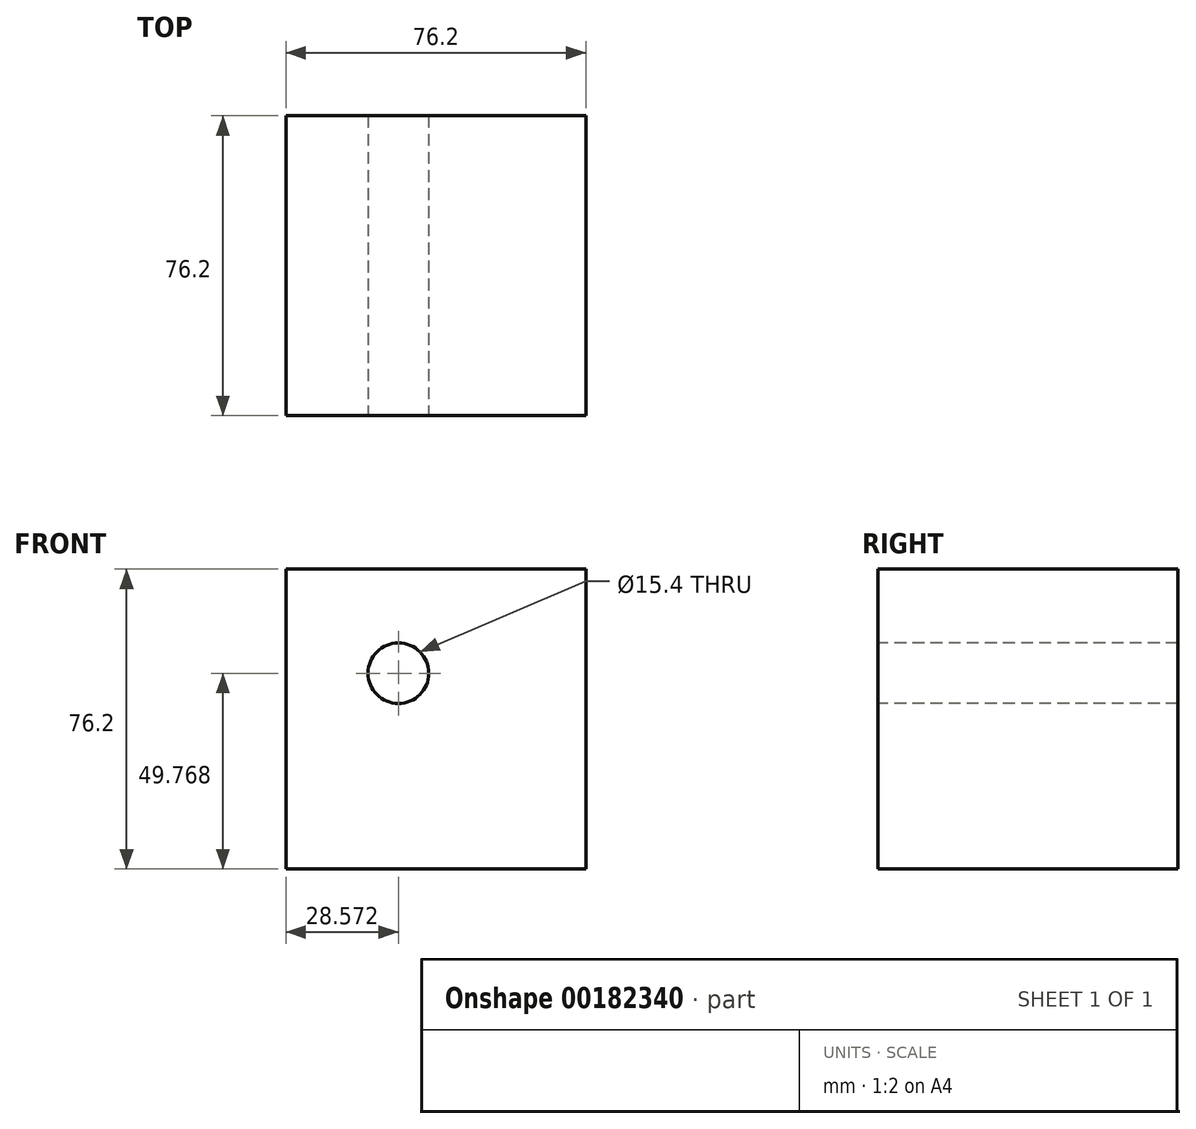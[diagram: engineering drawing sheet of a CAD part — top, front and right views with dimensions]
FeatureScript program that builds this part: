
annotation { "Feature Type Name" : "Feature", "Feature Type Description" : "" }
export const myFeature = defineFeature(function(context is Context, id is Id, definition is map)
    precondition{}
    {
        {
            var Q0;
            Q0=qCreatedBy(makeId("Front.planeOp"),FACE);
            var sketch = newSketch(context, id + "F0", { "sketchPlane" : qUnion([Q0])});
            skLineSegment(sketch, "E0", {"start": v(-37.52, -16.37) * mm, "end": v(38.68, -16.37) * mm});
            skLineSegment(sketch, "E1", {"start": v(38.68, 59.83) * mm, "end": v(38.68, -16.37) * mm});
            skLineSegment(sketch, "E2", {"start": v(-37.52, 59.83) * mm, "end": v(38.68, 59.83) * mm});
            skLineSegment(sketch, "E3", {"start": v(-37.52, 59.83) * mm, "end": v(-37.52, -16.37) * mm});
            skLineSegment(sketch, "E4", {"start": v(38.68, 59.83) * mm, "end": v(38.68, 59.83) * mm});
            skLineSegment(sketch, "E5", {"start": v(35.88, 59.83) * mm, "end": v(38.68, 59.83) * mm});
            skSolve(sketch);
        }
        {
            var Q0;
            Q0=makeQuery(id+"F0.imprint","IMPRINT",FACE,{"disambiguationData":[TD([[makeQuery(id+"F0.imprint","IMPRINT",EDGE,{"derivedFrom":sQuery(id+"F0.wireOp",EDGE,"E0")}),1.0]])]});
            var Q1;
            Q1 = qSketchRegion(id + "FBGqNr1LLSspxTy_0", true);
            extrude(context, id + "F1", {"entities" : qUnion([Q0, Q1]), "depth" : 76.2 * mm});
        }
        {
            var Q0;
            Q0=makeQuery(id+"F1.opExtrude","CAP_FACE",FACE,{"disambiguationData":[OSD([sQuery(id+"F0.wireOp",EDGE,"E0"),sQuery(id+"F0.wireOp",EDGE,"E1"),sQuery(id+"F0.wireOp",EDGE,"E2"),sQuery(id+"F0.wireOp",EDGE,"E3"),sQuery(id+"F0.wireOp",EDGE,"E5")])],"isStart":false});
            var sketch = newSketch(context, id + "F2", { "sketchPlane" : qUnion([Q0])});
            skCircle(sketch, "E6", {"center": v(-8.95, 33.4) * mm, "radius": 7.7 * mm});
            skSolve(sketch);
        }
        {
            var Q0;
            Q0=makeQuery(id+"F2.imprint","IMPRINT",FACE,{"disambiguationData":[TD([[makeQuery(id+"F2.imprint","IMPRINT",EDGE,{"derivedFrom":sQuery(id+"F2.wireOp",EDGE,"E6")}),1.0]])]});
            extrude(context, id + "F3", {"entities" : qUnion([Q0]), "operationType" : NewBodyOperationType.REMOVE, "oppositeDirection" : true, "depth" : 76.2 * mm});
        }
    });
